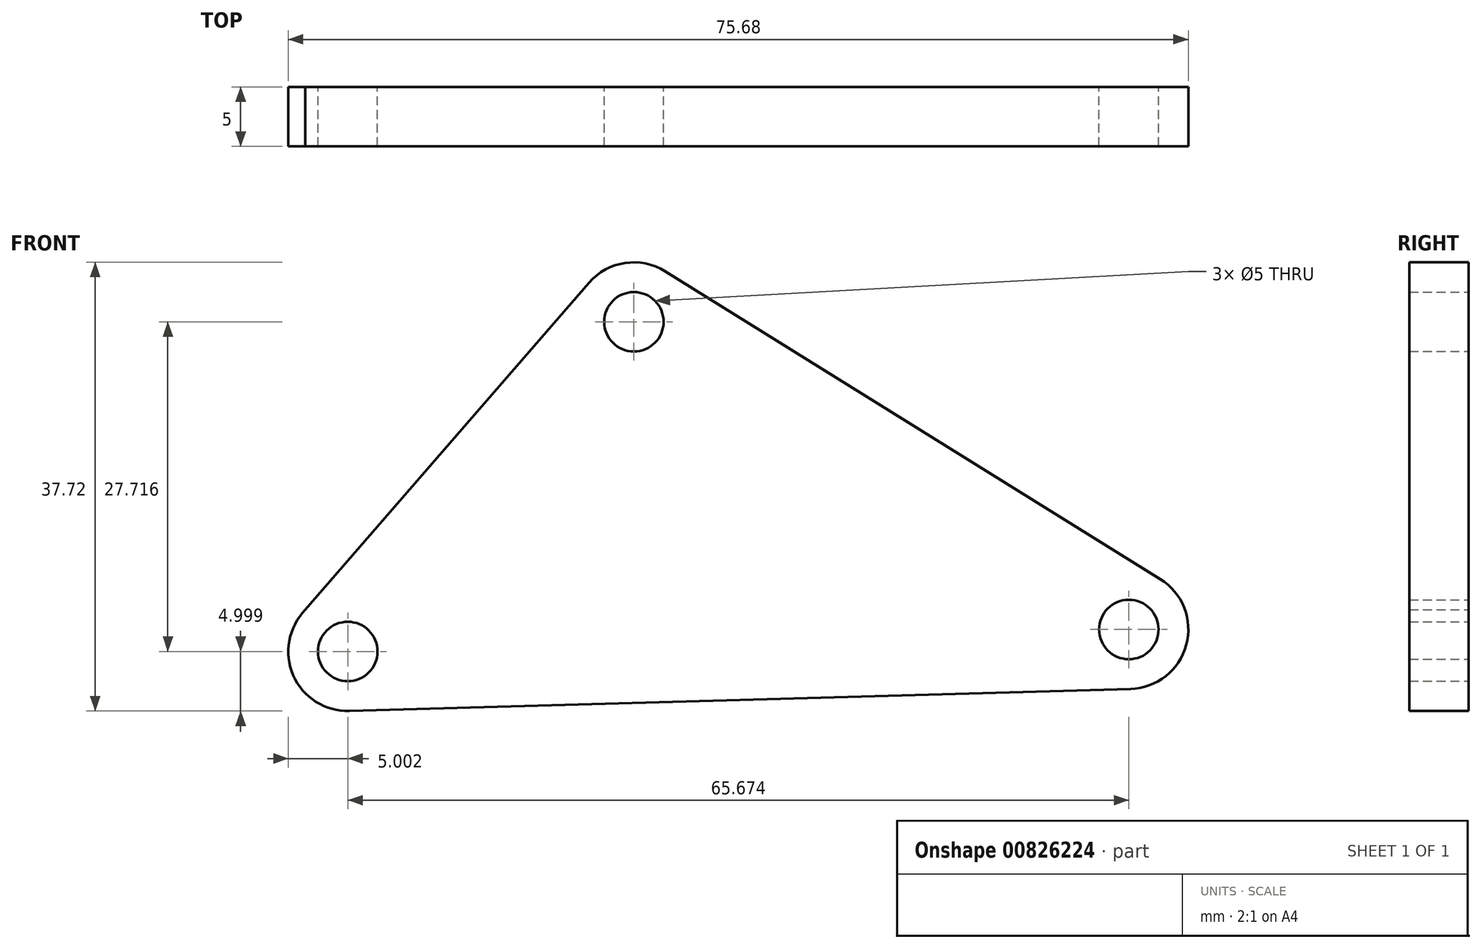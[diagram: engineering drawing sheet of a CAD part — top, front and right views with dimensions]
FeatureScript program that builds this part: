
annotation { "Feature Type Name" : "Feature", "Feature Type Description" : "" }
export const myFeature = defineFeature(function(context is Context, id is Id, definition is map)
    precondition{}
    {
        {
            var Q0;
            Q0=qCreatedBy(makeId("Front.planeOp"),FACE);
            var sketch = newSketch(context, id + "F0", { "sketchPlane" : qUnion([Q0])});
            skArc(sketch, "E0", {"start": v(-20.3, 0) * mm, "mid": v(-21.3, -5.5) * mm, "end": v(-16.59, -8.5) * mm});
            skArc(sketch, "E1", {"start": v(9.97, 28.46) * mm, "mid": v(6.58, 29.16) * mm, "end": v(3.55, 27.5) * mm});
            skArc(sketch, "E2", {"start": v(49.09, -6.65) * mm, "mid": v(53.77, -2.95) * mm, "end": v(51.59, 2.6) * mm});
            skLineSegment(sketch, "E3", {"start": v(-20.3, 0) * mm, "end": v(3.55, 27.5) * mm});
            skLineSegment(sketch, "E4", {"start": v(-16.59, -8.5) * mm, "end": v(49.09, -6.65) * mm});
            skLineSegment(sketch, "E5", {"start": v(9.97, 28.46) * mm, "end": v(51.59, 2.6) * mm});
            skCircle(sketch, "E6", {"center": v(7.33, 24.22) * mm, "radius": 2.5 * mm});
            skCircle(sketch, "E7", {"center": v(-16.73, -3.5) * mm, "radius": 2.5 * mm});
            skCircle(sketch, "E8", {"center": v(48.95, -1.65) * mm, "radius": 2.5 * mm});
            skSolve(sketch);
        }
        {
            var Q0;
            Q0 = qSketchRegion(id + "F0", true);
            extrude(context, id + "F1", {"entities" : qUnion([Q0]), "depth" : 5 * mm, "offsetDistance" : 25 * mm});
        }
    });
